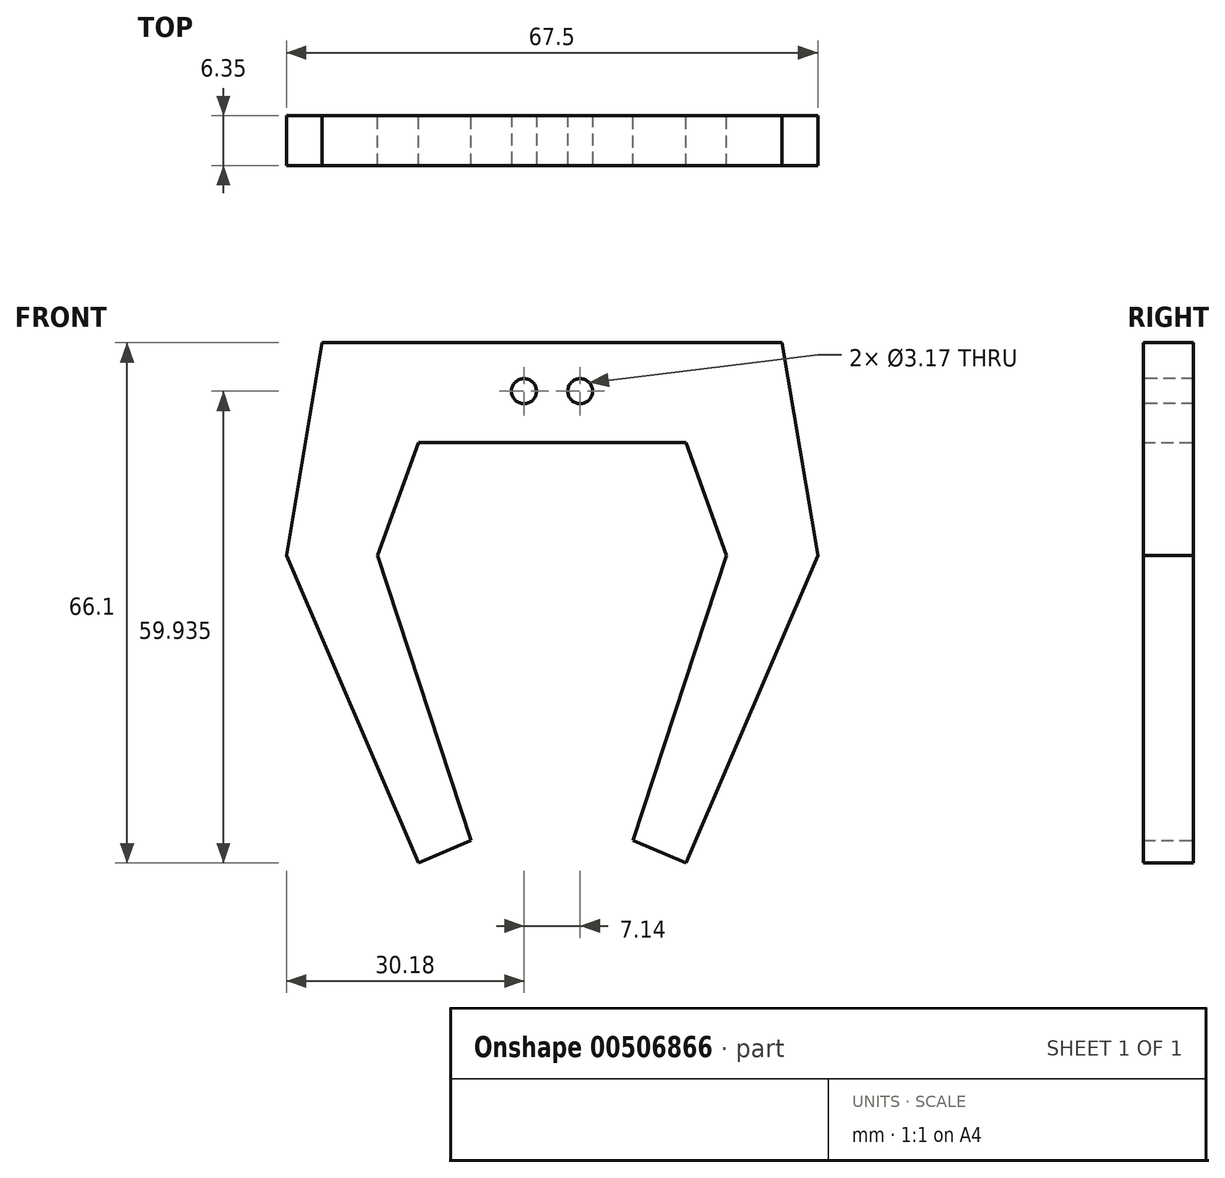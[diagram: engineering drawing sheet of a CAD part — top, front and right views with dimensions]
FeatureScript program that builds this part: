
annotation { "Feature Type Name" : "Feature", "Feature Type Description" : "" }
export const myFeature = defineFeature(function(context is Context, id is Id, definition is map)
    precondition{}
    {
        {
            var Q0;
            Q0=qCreatedBy(makeId("Front.planeOp"),FACE);
            var sketch = newSketch(context, id + "F0", { "sketchPlane" : qUnion([Q0])});
            skLineSegment(sketch, "E0", {"start": v(0, 27.03) * mm, "end": v(29.2, 27.03) * mm});
            skLineSegment(sketch, "E1", {"start": v(29.2, 27.03) * mm, "end": v(33.75, 0) * mm});
            skLineSegment(sketch, "E2", {"start": v(33.75, 0) * mm, "end": v(16.98, -39.07) * mm});
            skLineSegment(sketch, "E3", {"start": v(16.98, -39.07) * mm, "end": v(10.3, -36.2) * mm});
            skLineSegment(sketch, "E4", {"start": v(10.3, -36.2) * mm, "end": v(22.18, 0) * mm});
            skLineSegment(sketch, "E5", {"start": v(22.18, 0) * mm, "end": v(16.98, 14.33) * mm});
            skLineSegment(sketch, "E6", {"start": v(16.98, 14.33) * mm, "end": v(0, 14.33) * mm});
            skLineSegment(sketch, "E7", {"start": v(0, 14.33) * mm, "end": v(0, 27.03) * mm});
            skSolve(sketch);
        }
        {
            var Q0;
            Q0=makeQuery(id+"F0.imprint","IMPRINT",FACE,{"disambiguationData":[TD([[makeQuery(id+"F0.imprint","IMPRINT",EDGE,{"derivedFrom":sQuery(id+"F0.wireOp",EDGE,"E0")}),-1.0]])]});
            extrude(context, id + "F1", {"entities" : qUnion([Q0]), "depth" : 6.35 * mm, "offsetDistance" : 25.4 * mm});
        }
        {
            var Q0;
            {var subQ0=makeQuery(id+"F1.opExtrude","CAP_FACE",FACE,{"disambiguationData":[OSD([sQuery(id+"F0.wireOp",EDGE,"E0"),sQuery(id+"F0.wireOp",EDGE,"E1"),sQuery(id+"F0.wireOp",EDGE,"E2"),sQuery(id+"F0.wireOp",EDGE,"E3"),sQuery(id+"F0.wireOp",EDGE,"E4"),sQuery(id+"F0.wireOp",EDGE,"E5"),sQuery(id+"F0.wireOp",EDGE,"E6"),sQuery(id+"F0.wireOp",EDGE,"E7")])],"isStart":false});Q0=makeQuery(id+"F5aEJM5Ph6Br2Gn_1.boolean.opBoolean","MERGE",FACE,{"derivedFrom":[subQ0,makeQuery(id+"F5aEJM5Ph6Br2Gn_1.opPattern","COPY",FACE,{"derivedFrom":subQ0,"instanceName":"1"})]});}
            var sketch = newSketch(context, id + "F2", { "sketchPlane" : qUnion([Q0])});
            skCircle(sketch, "E8", {"center": v(3.57, 20.87) * mm, "radius": 2.14 * mm});
            skSolve(sketch);
        }
        {
            var Q0;
            Q0=sQuery(id+"F2.wireOp",VERTEX,"E8.center");
            var Q1;
            Q1=makeQuery(id+"F1.opExtrude","SWEPT_BODY",BODY,{"disambiguationData":[OSD([sQuery(id+"F0.wireOp",EDGE,"E0"),sQuery(id+"F0.wireOp",EDGE,"E1"),sQuery(id+"F0.wireOp",EDGE,"E2"),sQuery(id+"F0.wireOp",EDGE,"E3"),sQuery(id+"F0.wireOp",EDGE,"E4"),sQuery(id+"F0.wireOp",EDGE,"E5"),sQuery(id+"F0.wireOp",EDGE,"E6"),sQuery(id+"F0.wireOp",EDGE,"E7")])]});
            hole(context, id + "F3", {"style" : HoleStyle.SIMPLE, "endStyle" : HoleEndStyle.THROUGH, "holeDiameter" : 3.17 * mm, "isTappedThrough" : true, "tappedDepth" : 12.7 * mm, "tapClearance" : 3, "locations" : qUnion([Q0]), "scope" : qUnion([Q1])});
        }
        {
            var Q0;
            Q0=makeQuery(id+"F1.opExtrude","SWEPT_BODY",BODY,{"disambiguationData":[OSD([sQuery(id+"F0.wireOp",EDGE,"E0"),sQuery(id+"F0.wireOp",EDGE,"E1"),sQuery(id+"F0.wireOp",EDGE,"E2"),sQuery(id+"F0.wireOp",EDGE,"E3"),sQuery(id+"F0.wireOp",EDGE,"E4"),sQuery(id+"F0.wireOp",EDGE,"E5"),sQuery(id+"F0.wireOp",EDGE,"E6"),sQuery(id+"F0.wireOp",EDGE,"E7")])]});
            var Q1;
            Q1=qCreatedBy(makeId("Right.planeOp"),FACE);
            mirror(context, id + "F4", {"operationType" : NewBodyOperationType.ADD, "entities" : qUnion([Q0]), "mirrorPlane" : qUnion([Q1])});
        }
    });
